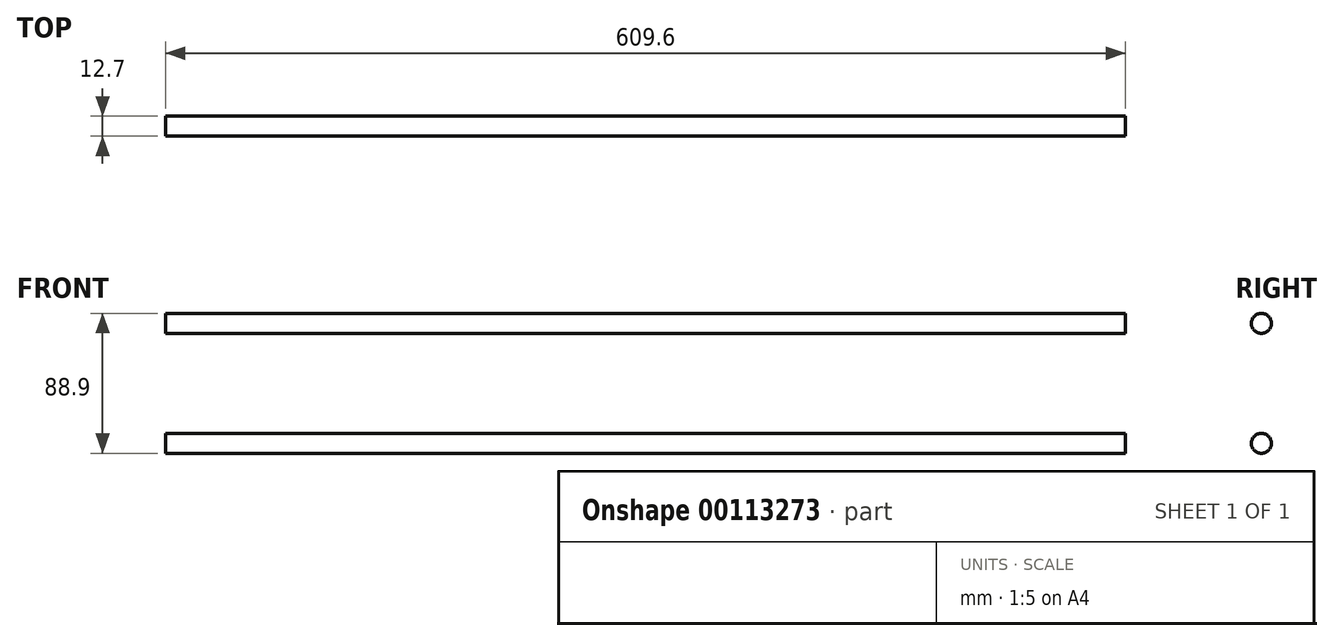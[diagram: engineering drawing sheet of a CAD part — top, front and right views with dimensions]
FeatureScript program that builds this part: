
annotation { "Feature Type Name" : "Feature", "Feature Type Description" : "" }
export const myFeature = defineFeature(function(context is Context, id is Id, definition is map)
    precondition{}
    {
        {
            var Q0;
            Q0=qCreatedBy(makeId("Right.planeOp"),FACE);
            var sketch = newSketch(context, id + "F0", { "sketchPlane" : qUnion([Q0])});
            skCircle(sketch, "E0", {"center": v(0, 38.1) * mm, "radius": 6.35 * mm});
            skCircle(sketch, "E1", {"center": v(0, -38.1) * mm, "radius": 6.35 * mm});
            skSolve(sketch);
        }
        {
            var Q0;
            Q0=makeQuery(id+"F0.imprint","IMPRINT",FACE,{"disambiguationData":[TD([[makeQuery(id+"F0.imprint","IMPRINT",EDGE,{"derivedFrom":sQuery(id+"F0.wireOp",EDGE,"E0")}),1.0]])]});
            var Q1;
            Q1=makeQuery(id+"F0.imprint","IMPRINT",FACE,{"disambiguationData":[TD([[makeQuery(id+"F0.imprint","IMPRINT",EDGE,{"derivedFrom":sQuery(id+"F0.wireOp",EDGE,"E1")}),1.0]])]});
            extrude(context, id + "F1", {"entities" : qUnion([Q0, Q1]), "depth" : 609.6 * mm});
        }
    });
